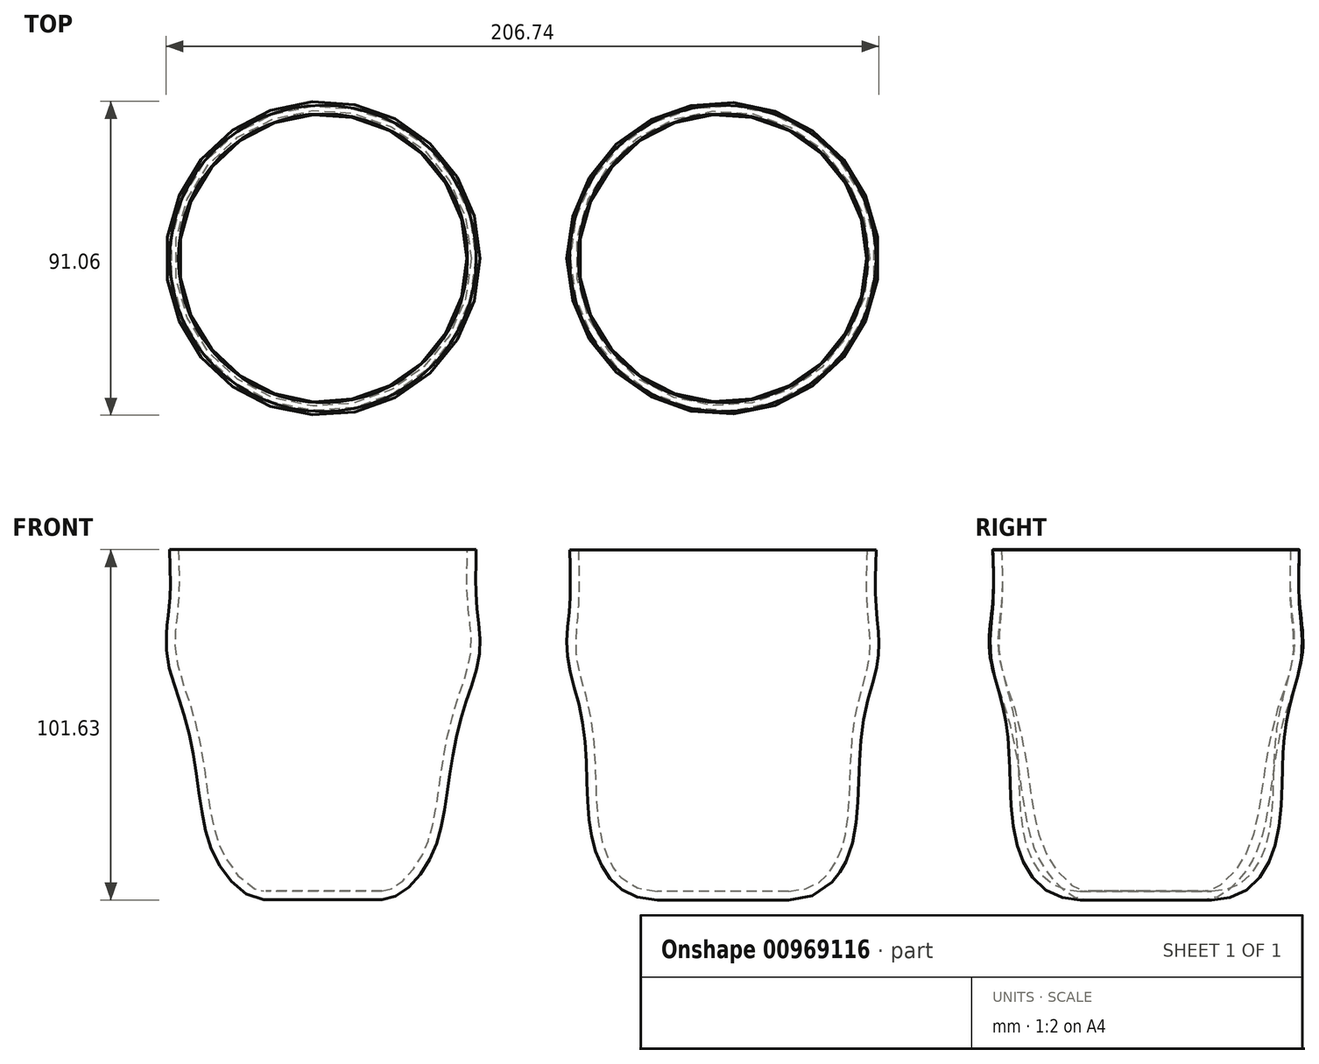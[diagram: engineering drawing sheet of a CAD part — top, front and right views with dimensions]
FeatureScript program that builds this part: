
annotation { "Feature Type Name" : "Feature", "Feature Type Description" : "" }
export const myFeature = defineFeature(function(context is Context, id is Id, definition is map)
    precondition{}
    {
        {
            var Q0;
            Q0=qCreatedBy(makeId("Front.planeOp"),FACE);
            var sketch = newSketch(context, id + "F0", { "sketchPlane" : qUnion([Q0])});
            skLineSegment(sketch, "E0", {"start": v(0, 0) * mm, "end": v(0, 71.05) * mm});
            skLineSegment(sketch, "E1", {"start": v(0, 0) * mm, "end": v(19.05, 0) * mm});
            skFitSpline(sketch, "E2", {"points": [v(19.05, 0) * mm, v(34.7, 9.18) * mm, v(39.04, 25.98) * mm, v(40.74, 51.95) * mm, v(45.07, 70.5) * mm, v(44.45, 85.18) * mm, v(44.45, 101.6) * mm], "startDerivative": vector(150.04, 0) * mm, "endDerivative": vector(2.7, 109.57) * mm});
            skLineSegment(sketch, "E3", {"start": v(44.45, 101.6) * mm, "end": v(0, 101.6) * mm});
            skLineSegment(sketch, "E4", {"start": v(0, 101.6) * mm, "end": v(0, 71.05) * mm});
            skSolve(sketch);
        }
        {
            var Q0;
            Q0=makeQuery(id+"F0.imprint","IMPRINT",FACE,{"disambiguationData":[TD([[makeQuery(id+"F0.imprint","IMPRINT",EDGE,{"derivedFrom":sQuery(id+"F0.wireOp",EDGE,"E0")}),-1.0]])]});
            var Q1;
            Q1=sQuery(id+"F0.wireOp",EDGE,"E0");
            revolve(context, id + "F1", {"surfaceOperationType" : NewSurfaceOperationType.NEW, "entities" : qUnion([Q0]), "axis" : qUnion([Q1]), "revolveType" : RevolveType.FULL});
        }
        {
            var Q0;
            Q0=makeQuery(id+"F1.opRevolve","SWEPT_FACE",FACE,{"disambiguationData":[OSD([sQuery(id+"F0.wireOp",EDGE,"E3")])]});
            shell(context, id + "F2", {"entities" : qUnion([Q0]), "thickness" : 2.54 * mm});
        }
        {
            var Q0;
            Q0=qCreatedBy(makeId("Front.planeOp"),FACE);
            var sketch = newSketch(context, id + "F3", { "sketchPlane" : qUnion([Q0])});
            skLineSegment(sketch, "E5", {"start": v(-115.97, 0.03) * mm, "end": v(-115.97, 71.09) * mm});
            skLineSegment(sketch, "E6", {"start": v(-115.97, 0.03) * mm, "end": v(-98.82, 0.03) * mm});
            skFitSpline(sketch, "E7", {"points": [v(-98.82, 0.03) * mm, v(-85.85, 10.19) * mm, v(-80.17, 29.61) * mm, v(-76, 52.63) * mm, v(-70.6, 71.46) * mm, v(-71.52, 87) * mm, v(-71.52, 101.63) * mm], "startDerivative": vector(87.98, 0) * mm, "endDerivative": vector(1.38, 89.16) * mm});
            skLineSegment(sketch, "E8", {"start": v(-71.52, 101.63) * mm, "end": v(-115.97, 101.63) * mm});
            skLineSegment(sketch, "E9", {"start": v(-115.97, 101.63) * mm, "end": v(-115.97, 71.09) * mm});
            skSolve(sketch);
        }
        {
            var Q0;
            Q0=makeQuery(id+"F3.imprint","IMPRINT",FACE,{"disambiguationData":[TD([[makeQuery(id+"F3.imprint","IMPRINT",EDGE,{"derivedFrom":sQuery(id+"F3.wireOp",EDGE,"E5")}),-1.0]])]});
            var Q1;
            Q1=sQuery(id+"F3.wireOp",EDGE,"E9");
            revolve(context, id + "F4", {"surfaceOperationType" : NewSurfaceOperationType.NEW, "entities" : qUnion([Q0]), "axis" : qUnion([Q1]), "revolveType" : RevolveType.FULL});
        }
        {
            var Q0;
            Q0=makeQuery(id+"F4.opRevolve","SWEPT_FACE",FACE,{"disambiguationData":[OSD([sQuery(id+"F3.wireOp",EDGE,"E8")])]});
            shell(context, id + "F5", {"entities" : qUnion([Q0]), "thickness" : 2.54 * mm});
        }
    });
